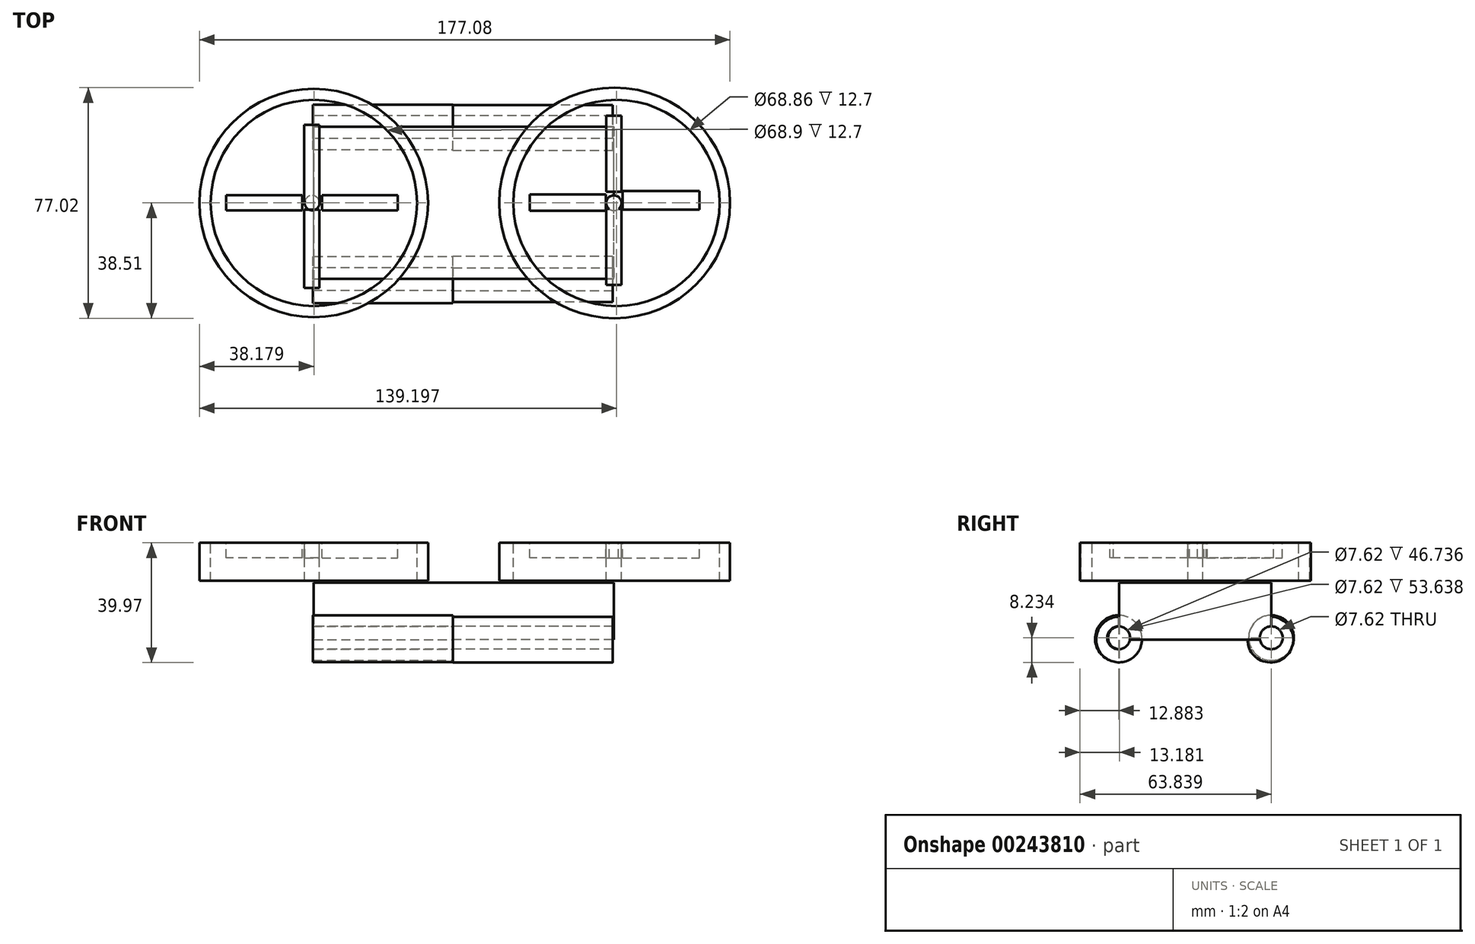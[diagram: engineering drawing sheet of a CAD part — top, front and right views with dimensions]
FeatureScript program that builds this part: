
annotation { "Feature Type Name" : "Feature", "Feature Type Description" : "" }
export const myFeature = defineFeature(function(context is Context, id is Id, definition is map)
    precondition{}
    {
        {
            var Q0;
            Q0=qCreatedBy(makeId("Front.planeOp"),FACE);
            var sketch = newSketch(context, id + "F0", { "sketchPlane" : qUnion([Q0])});
            skLineSegment(sketch, "E0.bottom", {"start": v(-46.49, -13.26) * mm, "end": v(53.64, -13.26) * mm});
            skLineSegment(sketch, "E0.top", {"start": v(-46.49, -32.33) * mm, "end": v(53.64, -32.33) * mm});
            skLineSegment(sketch, "E0.left", {"start": v(-46.49, -13.26) * mm, "end": v(-46.49, -32.33) * mm});
            skLineSegment(sketch, "E0.right", {"start": v(53.64, -13.26) * mm, "end": v(53.64, -32.33) * mm});
            skSolve(sketch);
        }
        {
            var Q0;
            Q0=makeQuery(id+"F0.imprint","IMPRINT",FACE,{"disambiguationData":[TD([[makeQuery(id+"F0.imprint","IMPRINT",EDGE,{"derivedFrom":sQuery(id+"F0.wireOp",EDGE,"E0.bottom")}),-1.0]])]});
            extrude(context, id + "F1", {"entities" : qUnion([Q0]), "endBound" : BoundingType.SYMMETRIC, "depth" : 50.8 * mm});
        }
        {
            var Q0;
            Q0=qCreatedBy(makeId("Right.planeOp"),FACE);
            var sketch = newSketch(context, id + "F2", { "sketchPlane" : qUnion([Q0])});
            skCircle(sketch, "E1", {"center": v(-25.48, -32.33) * mm, "radius": 7.61 * mm});
            skSolve(sketch);
        }
        {
            var Q0;
            Q0 = qSketchRegion(id + "F2", true);
            extrude(context, id + "F3", {"entities" : qUnion([Q0]), "operationType" : NewBodyOperationType.ADD, "depth" : 53.34 * mm});
        }
        {
            var Q0;
            Q0=qCreatedBy(makeId("Right.planeOp"),FACE);
            var sketch = newSketch(context, id + "F4", { "sketchPlane" : qUnion([Q0])});
            skCircle(sketch, "E2", {"center": v(-25.63, -32.03) * mm, "radius": 7.82 * mm});
            skSolve(sketch);
        }
        {
            var Q0;
            Q0 = qSketchRegion(id + "F4", true);
            extrude(context, id + "F5", {"entities" : qUnion([Q0]), "operationType" : NewBodyOperationType.ADD, "oppositeDirection" : true, "depth" : 46.74 * mm});
        }
        {
            var Q0;
            Q0=qCreatedBy(makeId("Right.planeOp"),FACE);
            var sketch = newSketch(context, id + "F6", { "sketchPlane" : qUnion([Q0])});
            skCircle(sketch, "E3", {"center": v(25.03, -32.33) * mm, "radius": 7.64 * mm});
            skSolve(sketch);
        }
        {
            var Q0;
            Q0 = qSketchRegion(id + "F6", true);
            extrude(context, id + "F7", {"entities" : qUnion([Q0]), "operationType" : NewBodyOperationType.ADD, "depth" : 53.34 * mm});
        }
        {
            var Q0;
            Q0=qCreatedBy(makeId("Right.planeOp"),FACE);
            var sketch = newSketch(context, id + "F8", { "sketchPlane" : qUnion([Q0])});
            skCircle(sketch, "E4", {"center": v(25.33, -31.74) * mm, "radius": 7.54 * mm});
            skSolve(sketch);
        }
        {
            var Q0;
            Q0 = qSketchRegion(id + "F8", true);
            extrude(context, id + "F9", {"entities" : qUnion([Q0]), "operationType" : NewBodyOperationType.ADD, "oppositeDirection" : true, "depth" : 46.74 * mm});
        }
        {
            var Q0;
            Q0=qCreatedBy(makeId("Top.planeOp"),FACE);
            var sketch = newSketch(context, id + "F10", { "sketchPlane" : qUnion([Q0])});
            skCircle(sketch, "E5", {"center": v(-46.49, 0) * mm, "radius": 38.15 * mm});
            skSolve(sketch);
        }
        {
            var Q0;
            Q0 = qSketchRegion(id + "F10", true);
            extrude(context, id + "F11", {"entities" : qUnion([Q0]), "operationType" : NewBodyOperationType.ADD, "oppositeDirection" : true, "depth" : 12.7 * mm});
        }
        {
            var Q0;
            Q0=qCreatedBy(makeId("Top.planeOp"),FACE);
            var sketch = newSketch(context, id + "F12", { "sketchPlane" : qUnion([Q0])});
            skCircle(sketch, "E6", {"center": v(53.94, 0) * mm, "radius": 38.51 * mm});
            skSolve(sketch);
        }
        {
            var Q0;
            Q0 = qSketchRegion(id + "F12", true);
            extrude(context, id + "F13", {"entities" : qUnion([Q0]), "oppositeDirection" : true, "depth" : 12.7 * mm});
        }
        {
            var Q0;
            Q0=qCreatedBy(makeId("Top.planeOp"),FACE);
            var sketch = newSketch(context, id + "F14", { "sketchPlane" : qUnion([Q0])});
            skCircle(sketch, "E7", {"center": v(-46.45, 0) * mm, "radius": 34.45 * mm});
            skSolve(sketch);
        }
        {
            var Q0;
            Q0 = qSketchRegion(id + "F14", true);
            extrude(context, id + "F15", {"entities" : qUnion([Q0]), "operationType" : NewBodyOperationType.REMOVE, "oppositeDirection" : true, "depth" : 12.7 * mm});
        }
        {
            var Q0;
            Q0=qCreatedBy(makeId("Top.planeOp"),FACE);
            var sketch = newSketch(context, id + "F16", { "sketchPlane" : qUnion([Q0])});
            skCircle(sketch, "E8", {"center": v(54.57, 0) * mm, "radius": 34.43 * mm});
            skSolve(sketch);
        }
        {
            var Q0;
            Q0 = qSketchRegion(id + "F16", true);
            extrude(context, id + "F17", {"entities" : qUnion([Q0]), "operationType" : NewBodyOperationType.REMOVE, "oppositeDirection" : true, "depth" : 12.7 * mm});
        }
        {
            var Q0;
            Q0=qCreatedBy(makeId("Top.planeOp"),FACE);
            var sketch = newSketch(context, id + "F18", { "sketchPlane" : qUnion([Q0])});
            skCircle(sketch, "E9", {"center": v(-47.05, 0) * mm, "radius": 2.48 * mm});
            skSolve(sketch);
        }
        {
            var Q0;
            Q0 = qSketchRegion(id + "F18", true);
            extrude(context, id + "F19", {"entities" : qUnion([Q0]), "oppositeDirection" : true, "depth" : 12.7 * mm});
        }
        {
            var Q0;
            Q0=qCreatedBy(makeId("Top.planeOp"),FACE);
            var sketch = newSketch(context, id + "F20", { "sketchPlane" : qUnion([Q0])});
            skCircle(sketch, "E10", {"center": v(53.67, 0) * mm, "radius": 2.53 * mm});
            skSolve(sketch);
        }
        {
            var Q0;
            Q0 = qSketchRegion(id + "F20", true);
            extrude(context, id + "F21", {"entities" : qUnion([Q0]), "oppositeDirection" : true, "depth" : 12.7 * mm});
        }
        {
            var Q0;
            Q0=qCreatedBy(makeId("Top.planeOp"),FACE);
            var sketch = newSketch(context, id + "F22", { "sketchPlane" : qUnion([Q0])});
            skLineSegment(sketch, "E11.bottom", {"start": v(-49.64, 26.1) * mm, "end": v(-44.56, 26.1) * mm});
            skLineSegment(sketch, "E11.top", {"start": v(-49.64, 0.7) * mm, "end": v(-44.56, 0.7) * mm});
            skLineSegment(sketch, "E11.left", {"start": v(-49.64, 26.1) * mm, "end": v(-49.64, 0.7) * mm});
            skLineSegment(sketch, "E11.right", {"start": v(-44.56, 26.1) * mm, "end": v(-44.56, 0.7) * mm});
            skSolve(sketch);
        }
        {
            var Q0;
            Q0 = qSketchRegion(id + "F22", true);
            extrude(context, id + "F23", {"entities" : qUnion([Q0]), "operationType" : NewBodyOperationType.ADD, "oppositeDirection" : true, "depth" : 5.08 * mm});
        }
        {
            var Q0;
            Q0=qCreatedBy(makeId("Top.planeOp"),FACE);
            var sketch = newSketch(context, id + "F24", { "sketchPlane" : qUnion([Q0])});
            skLineSegment(sketch, "E12.bottom", {"start": v(-50.32, 2.53) * mm, "end": v(-75.72, 2.53) * mm});
            skLineSegment(sketch, "E12.top", {"start": v(-50.32, -2.55) * mm, "end": v(-75.72, -2.55) * mm});
            skLineSegment(sketch, "E12.left", {"start": v(-50.32, 2.53) * mm, "end": v(-50.32, -2.55) * mm});
            skLineSegment(sketch, "E12.right", {"start": v(-75.72, 2.53) * mm, "end": v(-75.72, -2.55) * mm});
            skSolve(sketch);
        }
        {
            var Q0;
            Q0 = qSketchRegion(id + "F24", true);
            extrude(context, id + "F25", {"entities" : qUnion([Q0]), "oppositeDirection" : true, "depth" : 5.08 * mm});
        }
        {
            var Q0;
            Q0=qCreatedBy(makeId("Top.planeOp"),FACE);
            var sketch = newSketch(context, id + "F26", { "sketchPlane" : qUnion([Q0])});
            skLineSegment(sketch, "E13.bottom", {"start": v(-49.73, -2.23) * mm, "end": v(-44.66, -2.23) * mm});
            skLineSegment(sketch, "E13.top", {"start": v(-49.73, -28.46) * mm, "end": v(-44.66, -28.46) * mm});
            skLineSegment(sketch, "E13.left", {"start": v(-49.73, -2.23) * mm, "end": v(-49.73, -28.46) * mm});
            skLineSegment(sketch, "E13.right", {"start": v(-44.66, -2.23) * mm, "end": v(-44.66, -28.46) * mm});
            skSolve(sketch);
        }
        {
            var Q0;
            Q0 = qSketchRegion(id + "F26", true);
            extrude(context, id + "F27", {"entities" : qUnion([Q0]), "oppositeDirection" : true, "depth" : 5.08 * mm});
        }
        {
            var Q0;
            Q0=qCreatedBy(makeId("Top.planeOp"),FACE);
            var sketch = newSketch(context, id + "F28", { "sketchPlane" : qUnion([Q0])});
            skLineSegment(sketch, "E14.bottom", {"start": v(-43.77, 2.53) * mm, "end": v(-18.44, 2.53) * mm});
            skLineSegment(sketch, "E14.top", {"start": v(-43.77, -2.53) * mm, "end": v(-18.44, -2.53) * mm});
            skLineSegment(sketch, "E14.left", {"start": v(-43.77, 2.53) * mm, "end": v(-43.77, -2.53) * mm});
            skLineSegment(sketch, "E14.right", {"start": v(-18.44, 2.53) * mm, "end": v(-18.44, -2.53) * mm});
            skSolve(sketch);
        }
        {
            var Q0;
            Q0 = qSketchRegion(id + "F28", true);
            extrude(context, id + "F29", {"entities" : qUnion([Q0]), "oppositeDirection" : true, "depth" : 5.08 * mm});
        }
        {
            var Q0;
            Q0=qCreatedBy(makeId("Top.planeOp"),FACE);
            var sketch = newSketch(context, id + "F30", { "sketchPlane" : qUnion([Q0])});
            skLineSegment(sketch, "E15.bottom", {"start": v(51.1, 3.69) * mm, "end": v(56.18, 3.69) * mm});
            skLineSegment(sketch, "E15.top", {"start": v(51.1, 29.09) * mm, "end": v(56.18, 29.09) * mm});
            skLineSegment(sketch, "E15.left", {"start": v(51.1, 3.69) * mm, "end": v(51.1, 29.09) * mm});
            skLineSegment(sketch, "E15.right", {"start": v(56.18, 3.69) * mm, "end": v(56.18, 29.09) * mm});
            skSolve(sketch);
        }
        {
            var Q0;
            Q0 = qSketchRegion(id + "F30", true);
            extrude(context, id + "F31", {"entities" : qUnion([Q0]), "oppositeDirection" : true, "depth" : 5.08 * mm});
        }
        {
            var Q0;
            Q0=qCreatedBy(makeId("Top.planeOp"),FACE);
            var sketch = newSketch(context, id + "F32", { "sketchPlane" : qUnion([Q0])});
            skLineSegment(sketch, "E16.bottom", {"start": v(51.03, 2.9) * mm, "end": v(25.63, 2.9) * mm});
            skLineSegment(sketch, "E16.top", {"start": v(51.03, -2.6) * mm, "end": v(25.63, -2.6) * mm});
            skLineSegment(sketch, "E16.left", {"start": v(51.03, 2.9) * mm, "end": v(51.03, -2.6) * mm});
            skLineSegment(sketch, "E16.right", {"start": v(25.63, 2.9) * mm, "end": v(25.63, -2.6) * mm});
            skSolve(sketch);
        }
        {
            var Q0;
            Q0 = qSketchRegion(id + "F32", true);
            extrude(context, id + "F33", {"entities" : qUnion([Q0]), "oppositeDirection" : true, "depth" : 5.08 * mm});
        }
        {
            var Q0;
            Q0=qCreatedBy(makeId("Top.planeOp"),FACE);
            var sketch = newSketch(context, id + "F34", { "sketchPlane" : qUnion([Q0])});
            skLineSegment(sketch, "E17.bottom", {"start": v(51.13, -2.02) * mm, "end": v(56.21, -2.02) * mm});
            skLineSegment(sketch, "E17.top", {"start": v(51.13, -27.42) * mm, "end": v(56.21, -27.42) * mm});
            skLineSegment(sketch, "E17.left", {"start": v(51.13, -2.02) * mm, "end": v(51.13, -27.42) * mm});
            skLineSegment(sketch, "E17.right", {"start": v(56.21, -2.02) * mm, "end": v(56.21, -27.42) * mm});
            skSolve(sketch);
        }
        {
            var Q0;
            Q0 = qSketchRegion(id + "F34", true);
            extrude(context, id + "F35", {"entities" : qUnion([Q0]), "operationType" : NewBodyOperationType.ADD, "oppositeDirection" : true, "depth" : 5.08 * mm});
        }
        {
            var Q0;
            Q0=qCreatedBy(makeId("Top.planeOp"),FACE);
            var sketch = newSketch(context, id + "F36", { "sketchPlane" : qUnion([Q0])});
            skLineSegment(sketch, "E18.bottom", {"start": v(56.65, 4.02) * mm, "end": v(82.28, 4.02) * mm});
            skLineSegment(sketch, "E18.top", {"start": v(56.65, -2.23) * mm, "end": v(82.28, -2.23) * mm});
            skLineSegment(sketch, "E18.left", {"start": v(56.65, 4.02) * mm, "end": v(56.65, -2.23) * mm});
            skLineSegment(sketch, "E18.right", {"start": v(82.28, 4.02) * mm, "end": v(82.28, -2.23) * mm});
            skSolve(sketch);
        }
        {
            var Q0;
            Q0 = qSketchRegion(id + "F36", true);
            extrude(context, id + "F37", {"entities" : qUnion([Q0]), "oppositeDirection" : true, "depth" : 5.08 * mm});
        }
        {
            var Q0;
            Q0=qCreatedBy(makeId("Right.planeOp"),FACE);
            var sketch = newSketch(context, id + "F38", { "sketchPlane" : qUnion([Q0])});
            skCircle(sketch, "E19", {"center": v(-25.33, -31.74) * mm, "radius": 3.81 * mm});
            skSolve(sketch);
        }
        {
            var Q0;
            Q0 = qSketchRegion(id + "F38", true);
            extrude(context, id + "F39", {"entities" : qUnion([Q0]), "operationType" : NewBodyOperationType.REMOVE, "endBound" : BoundingType.THROUGH_ALL, "oppositeDirection" : true, "depth" : 25.4 * mm});
        }
        {
            var Q0;
            Q0=qCreatedBy(makeId("Right.planeOp"),FACE);
            var sketch = newSketch(context, id + "F40", { "sketchPlane" : qUnion([Q0])});
            skCircle(sketch, "E20", {"center": v(-25.63, -31.74) * mm, "radius": 3.81 * mm});
            skSolve(sketch);
        }
        {
            var Q0;
            Q0 = qSketchRegion(id + "F40", true);
            extrude(context, id + "F41", {"entities" : qUnion([Q0]), "operationType" : NewBodyOperationType.REMOVE, "endBound" : BoundingType.THROUGH_ALL, "depth" : 25.4 * mm});
        }
        {
            var Q0;
            Q0=qCreatedBy(makeId("Right.planeOp"),FACE);
            var sketch = newSketch(context, id + "F42", { "sketchPlane" : qUnion([Q0])});
            skCircle(sketch, "E21", {"center": v(25.33, -31.74) * mm, "radius": 3.81 * mm});
            skSolve(sketch);
        }
        {
            var Q0;
            Q0 = qSketchRegion(id + "F42", true);
            extrude(context, id + "F43", {"entities" : qUnion([Q0]), "operationType" : NewBodyOperationType.REMOVE, "endBound" : BoundingType.THROUGH_ALL, "depth" : 25.4 * mm});
        }
        {
            var Q0;
            Q0=qCreatedBy(makeId("Right.planeOp"),FACE);
            var sketch = newSketch(context, id + "F44", { "sketchPlane" : qUnion([Q0])});
            skCircle(sketch, "E22", {"center": v(25.33, -31.74) * mm, "radius": 3.81 * mm});
            skSolve(sketch);
        }
        {
            var Q0;
            Q0 = qSketchRegion(id + "F44", true);
            extrude(context, id + "F45", {"entities" : qUnion([Q0]), "operationType" : NewBodyOperationType.REMOVE, "endBound" : BoundingType.THROUGH_ALL, "oppositeDirection" : true, "depth" : 25.4 * mm});
        }
    });
